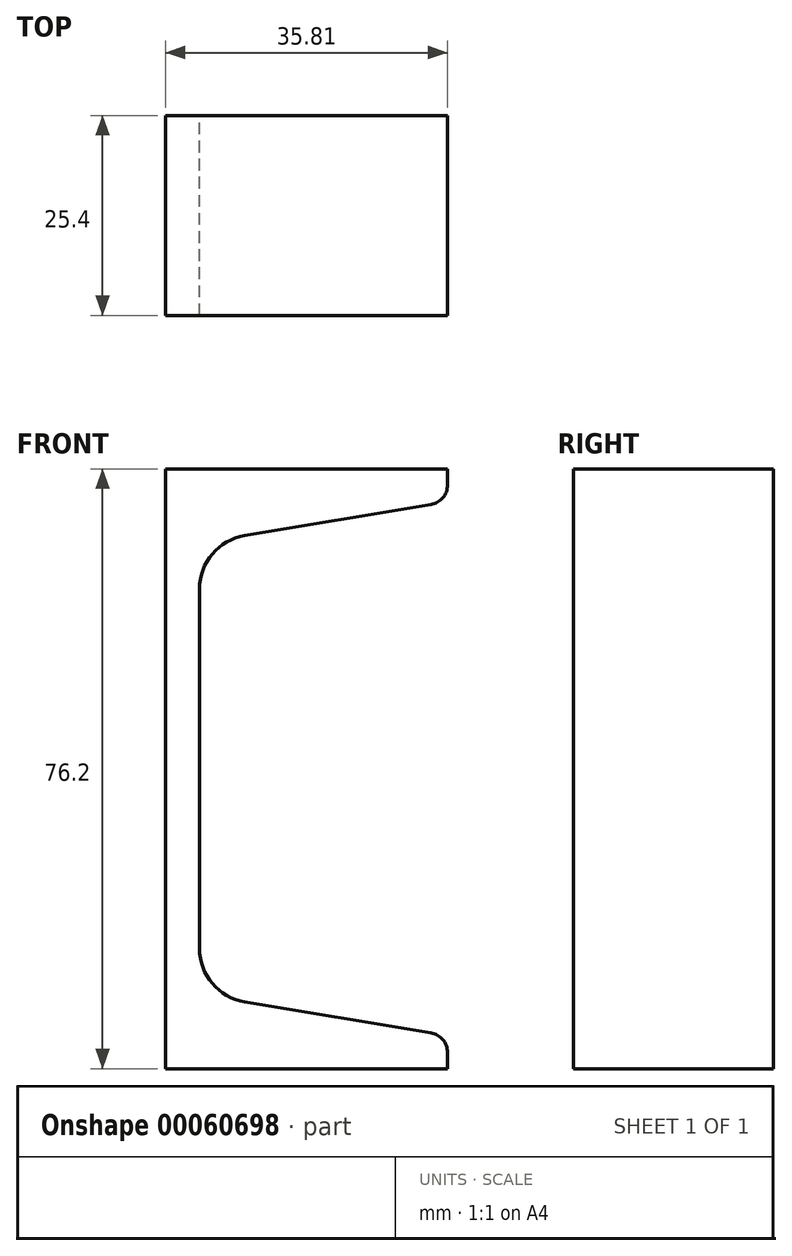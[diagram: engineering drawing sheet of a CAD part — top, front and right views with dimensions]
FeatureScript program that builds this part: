
annotation { "Feature Type Name" : "Feature", "Feature Type Description" : "" }
export const myFeature = defineFeature(function(context is Context, id is Id, definition is map)
    precondition{}
    {
        {
            var Q0;
            Q0=qCreatedBy(makeId("Front.planeOp"),FACE);
            var sketch = newSketch(context, id + "F0", { "sketchPlane" : qUnion([Q0])});
            skLineSegment(sketch, "E0", {"start": v(0, 38.1) * mm, "end": v(0, -38.1) * mm});
            skLineSegment(sketch, "E1", {"start": v(0, 38.1) * mm, "end": v(35.81, 38.1) * mm});
            skLineSegment(sketch, "E2", {"start": v(35.81, 38.1) * mm, "end": v(35.81, 36.07) * mm});
            skLineSegment(sketch, "E3", {"start": v(0, -38.1) * mm, "end": v(35.81, -38.1) * mm});
            skLineSegment(sketch, "E4", {"start": v(35.81, -38.1) * mm, "end": v(35.81, -36.07) * mm});
            skLineSegment(sketch, "E5", {"start": v(33.7, 33.56) * mm, "end": v(10.05, 29.62) * mm});
            skLineSegment(sketch, "E6", {"start": v(4.32, 22.86) * mm, "end": v(4.32, -22.86) * mm});
            skLineSegment(sketch, "E7", {"start": v(10.05, -29.62) * mm, "end": v(33.7, -33.56) * mm});
            skPoint(sketch, "E8", {"position": v(4.32, 0) * mm});
            skPoint(sketch, "E9.visualSharp", {"position": v(35.81, 33.92) * mm});
            skArc(sketch, "E9.filletArc", {"start": v(33.7, 33.56) * mm, "mid": v(35.21, 34.43) * mm, "end": v(35.81, 36.07) * mm});
            skPoint(sketch, "E10.visualSharp", {"position": v(35.81, -33.92) * mm});
            skArc(sketch, "E10.filletArc", {"start": v(35.81, -36.07) * mm, "mid": v(35.21, -34.43) * mm, "end": v(33.7, -33.56) * mm});
            skPoint(sketch, "E11.visualSharp", {"position": v(4.32, 28.67) * mm});
            skArc(sketch, "E11.filletArc", {"start": v(10.05, 29.62) * mm, "mid": v(5.94, 27.3) * mm, "end": v(4.32, 22.86) * mm});
            skPoint(sketch, "E12.visualSharp", {"position": v(4.32, -28.67) * mm});
            skArc(sketch, "E12.filletArc", {"start": v(4.32, -22.86) * mm, "mid": v(5.94, -27.3) * mm, "end": v(10.05, -29.62) * mm});
            skSolve(sketch);
        }
        {
            var Q0;
            Q0=makeQuery(id+"F0.imprint","IMPRINT",FACE,{"disambiguationData":[TD([[makeQuery(id+"F0.imprint","IMPRINT",EDGE,{"derivedFrom":sQuery(id+"F0.wireOp",EDGE,"E0")}),1.0]])]});
            extrude(context, id + "F1", {"entities" : qUnion([Q0]), "endBound" : BoundingType.SYMMETRIC, "depth" : 25.4 * mm});
        }
    });
